# Revit family: KBE d=400_Precast-Console Beam_Spæncom
name_source: partatom
category: Structural Framing
revit_build: Autodesk Revit 2014 (Build: 20130308_1515(x64)
units: mm (PartAtom-declared; Revit-internal decimal feet)

## types (8) — shared parameters
Base width = 360 mm  [stored 1.1811 ft]
Height console = 400 mm  [stored 1.31234 ft]
Height element = 900 mm
Manufacturer = Spæncom
Width (bjælkekroppen) = 260 mm  [stored 0.853018 ft]
Width console = 150 mm

## per-type parameters (varying)
| type | Height (bjælkekroppen) |
| KBE 58/18 | 180 mm  [stored 0.590551 ft] |
| KBE 62/22 | 220 mm  [stored 0.721785 ft] |
| KBE 67/27 | 270 mm  [stored 0.885827 ft] |
| KBE 70/30 | 300 mm |
| KBE 72/32 | 320 mm  [stored 1.04987 ft] |
| KBE 77/37 | 370 mm  [stored 1.21391 ft] |
| KBE 80/40 | 400 mm  [stored 1.31234 ft] |
| KBE 90/50 | 500 mm  [stored 1.64042 ft] |

note: column(s) folded — value = type name in every type: Model

note: [stored X ft] marks values corroborated as IEEE doubles in the binary element streams (Revit-internal decimal feet)

## geometry (parser evidence)
native form markers: Sweep x1
no freeform markers — native parametric forms only
